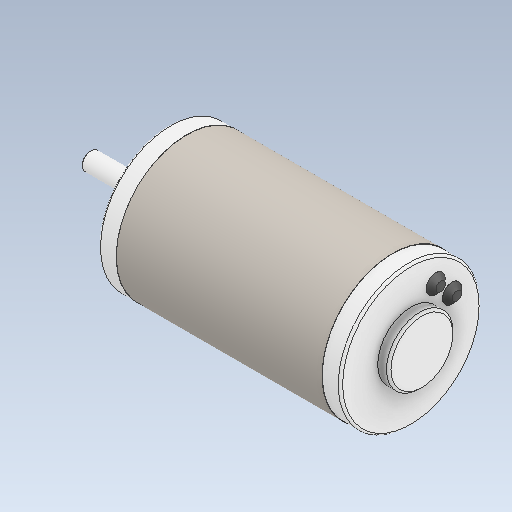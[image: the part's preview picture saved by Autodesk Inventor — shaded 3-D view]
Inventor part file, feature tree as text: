
AUTODESK INVENTOR PART (.ipt)
format: ipt  version: 2020 (Build 240168000, 168)  size: 168,960 bytes
history: native  units: in
note: dims shown in document units (in); Inventor stores cm internally (conversion verified against a paired STEP export)
features: chamfer x1
ambient origin geometry x8: Origin, YZ Plane, XZ Plane, XY Plane, X Axis, Y Axis, Z Axis, Center Point
bodies: Solid1 (feature_tree)
feature tree (1):
  chamfer  "Chamfer3"  [1 undecoded]
note: 1 required parameter value undecoded (feature->parameter linkage not recoverable at this tier; creation-order binding heuristic only, values carry confidence <= 0.55)
